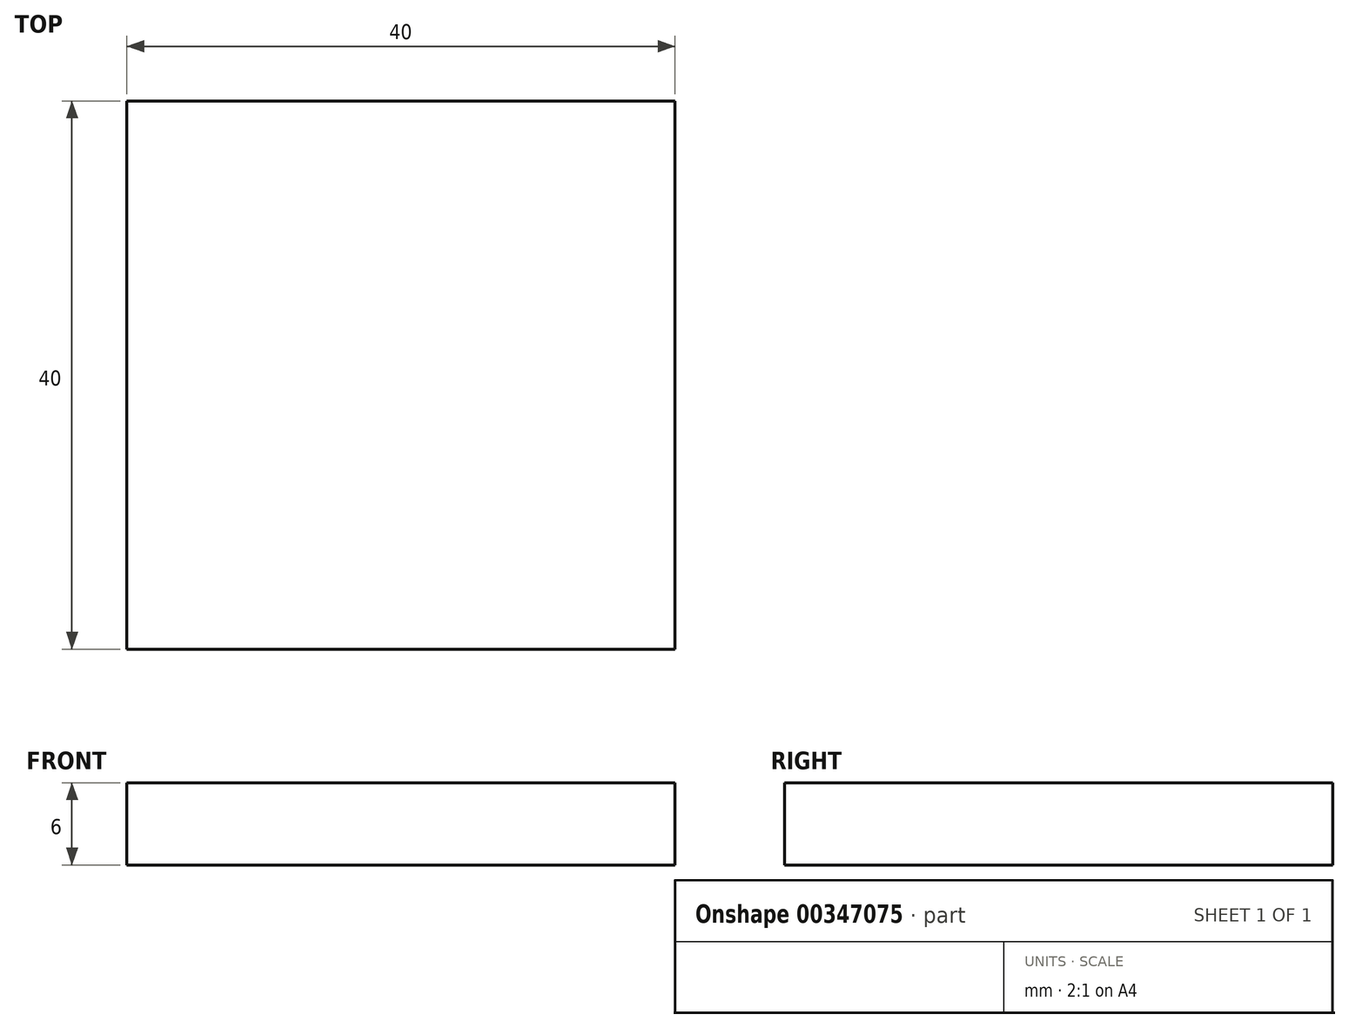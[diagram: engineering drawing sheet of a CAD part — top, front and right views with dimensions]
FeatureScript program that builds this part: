
annotation { "Feature Type Name" : "Feature", "Feature Type Description" : "" }
export const myFeature = defineFeature(function(context is Context, id is Id, definition is map)
    precondition{}
    {
        {
            var Q0;
            Q0=qCreatedBy(makeId("Top.planeOp"),FACE);
            var sketch = newSketch(context, id + "F0", { "sketchPlane" : qUnion([Q0])});
            skLineSegment(sketch, "E0.bottom", {"start": v(20, -20) * mm, "end": v(-20, -20) * mm});
            skLineSegment(sketch, "E0.top", {"start": v(20, 20) * mm, "end": v(-20, 20) * mm});
            skLineSegment(sketch, "E0.left", {"start": v(20, -20) * mm, "end": v(20, 20) * mm});
            skLineSegment(sketch, "E0.right", {"start": v(-20, -20) * mm, "end": v(-20, 20) * mm});
            skPoint(sketch, "E0.middle", {"position": v(0, 0) * mm});
            skSolve(sketch);
        }
        {
            var Q0;
            Q0 = qSketchRegion(id + "F0", true);
            extrude(context, id + "F1", {"entities" : qUnion([Q0]), "depth" : 6 * mm});
        }
    });
